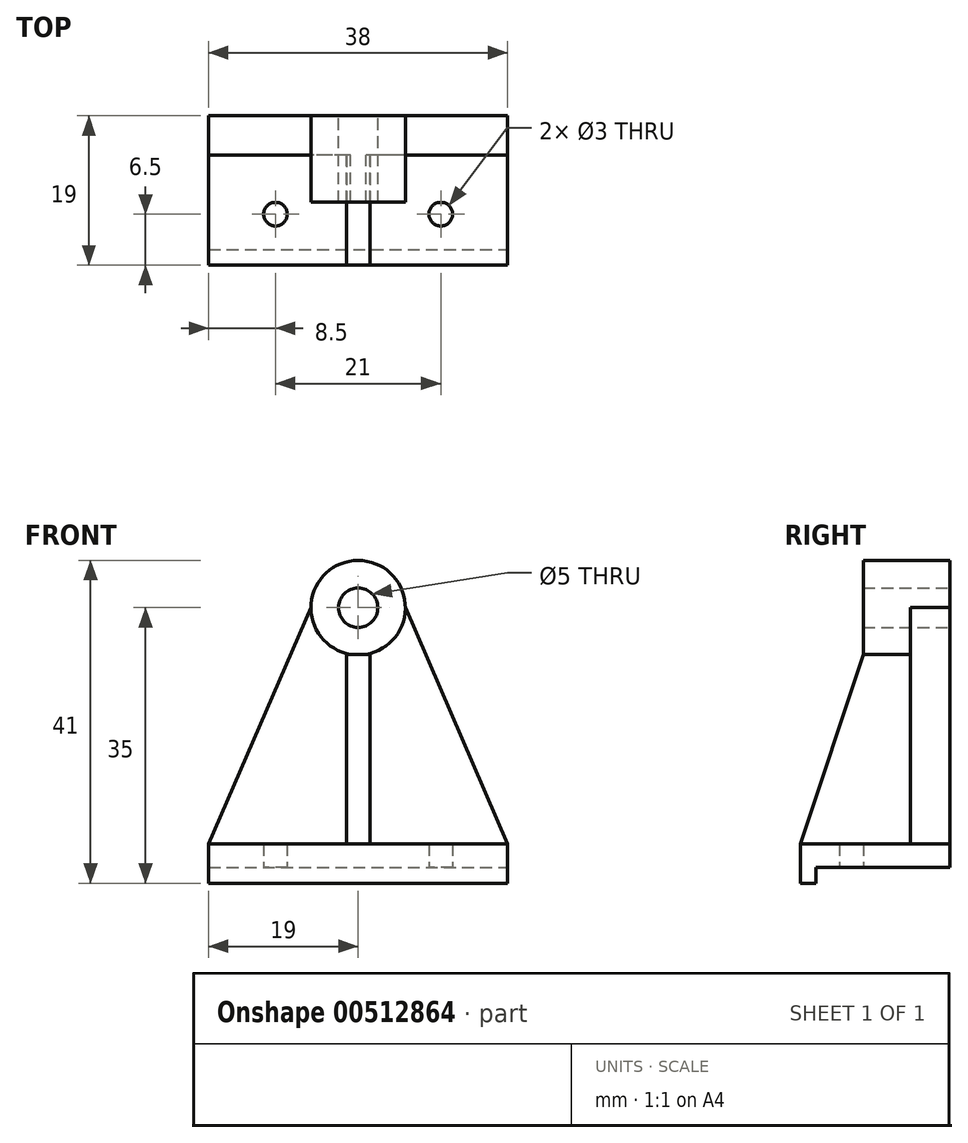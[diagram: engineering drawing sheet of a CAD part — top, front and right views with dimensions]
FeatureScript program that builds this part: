
annotation { "Feature Type Name" : "Feature", "Feature Type Description" : "" }
export const myFeature = defineFeature(function(context is Context, id is Id, definition is map)
    precondition{}
    {
        {
            var Q0;
            Q0=qCreatedBy(makeId("Top.planeOp"),FACE);
            var sketch = newSketch(context, id + "F0", { "sketchPlane" : qUnion([Q0])});
            skLineSegment(sketch, "E0.bottom", {"start": v(19, -9.5) * mm, "end": v(-19, -9.5) * mm});
            skLineSegment(sketch, "E0.top", {"start": v(19, 9.5) * mm, "end": v(-19, 9.5) * mm});
            skLineSegment(sketch, "E0.left", {"start": v(19, -9.5) * mm, "end": v(19, 9.5) * mm});
            skLineSegment(sketch, "E0.right", {"start": v(-19, -9.5) * mm, "end": v(-19, 9.5) * mm});
            skPoint(sketch, "E0.middle", {"position": v(0, 0) * mm});
            skCircle(sketch, "E1", {"center": v(10.5, -3) * mm, "radius": 1.5 * mm});
            skLineSegment(sketch, "E2", {"start": v(0, 0) * mm, "end": v(0, -4.4) * mm, "construction": true});
            skCircle(sketch, "E3.MirrorC", {"center": v(-10.5, -3) * mm, "radius": 1.5 * mm});
            skSolve(sketch);
        }
        {
            var Q0;
            Q0 = qSketchRegion(id + "F0", true);
            extrude(context, id + "F1", {"entities" : qUnion([Q0]), "depth" : 3 * mm});
        }
        {
            var Q0;
            Q0=makeQuery(id+"F1.opExtrude","SWEPT_FACE",FACE,{"disambiguationData":[OSD([sQuery(id+"F0.wireOp",EDGE,"E0.left")])]});
            var sketch = newSketch(context, id + "F2", { "sketchPlane" : qUnion([Q0])});
            skLineSegment(sketch, "E4.bottom", {"start": v(-9.5, 0) * mm, "end": v(-7.5, 0) * mm});
            skLineSegment(sketch, "E4.top", {"start": v(-9.5, -2) * mm, "end": v(-7.5, -2) * mm});
            skLineSegment(sketch, "E4.left", {"start": v(-9.5, 0) * mm, "end": v(-9.5, -2) * mm});
            skLineSegment(sketch, "E4.right", {"start": v(-7.5, 0) * mm, "end": v(-7.5, -2) * mm});
            skSolve(sketch);
        }
        {
            var Q0;
            Q0 = qSketchRegion(id + "F2", true);
            extrude(context, id + "F3", {"entities" : qUnion([Q0]), "operationType" : NewBodyOperationType.ADD, "oppositeDirection" : true, "depth" : 38 * mm});
        }
        {
            var Q0;
            Q0=makeQuery(id+"F1.opExtrude","SWEPT_FACE",FACE,{"disambiguationData":[OSD([sQuery(id+"F0.wireOp",EDGE,"E0.top")])]});
            var sketch = newSketch(context, id + "F4", { "sketchPlane" : qUnion([Q0])});
            skCircle(sketch, "E5", {"center": v(0, 33) * mm, "radius": 2.5 * mm});
            skCircle(sketch, "E6", {"center": v(0, 33) * mm, "radius": 6 * mm});
            skLineSegment(sketch, "E7", {"start": v(-19, 3) * mm, "end": v(-6, 33) * mm});
            skLineSegment(sketch, "E8", {"start": v(-6, 33) * mm, "end": v(6, 33) * mm});
            skLineSegment(sketch, "E9", {"start": v(6, 33) * mm, "end": v(19, 3) * mm});
            skSolve(sketch);
        }
        {
            var Q0;
            {var subQ1=sQuery(id+"F4.wireOp",EDGE,"E7");Q0=makeQuery(id+"F4.imprint","IMPRINT",FACE,{"disambiguationData":[TD([[makeQuery(id+"F4.imprint","IMPRINT",EDGE,{"derivedFrom":subQ1}),-1.0]])]});}
            extrude(context, id + "F5", {"entities" : qUnion([Q0]), "operationType" : NewBodyOperationType.ADD, "oppositeDirection" : true, "depth" : 5 * mm});
        }
        {
            var Q0;
            {var subQ0=sQuery(id+"F4.wireOp",EDGE,"E8");var subQ1=sQuery(id+"F4.wireOp",EDGE,"E5");var subQ2=makeQuery(id+"F4.imprint","INTERSECT",VERTEX,{"disambiguationData":[OD(0.0)],"derivedFrom":[subQ1,subQ0]});Q0=makeQuery(id+"F4.imprint","IMPRINT",FACE,{"disambiguationData":[TD([[makeQuery(id+"F4.imprint","IMPRINT",EDGE,{"disambiguationData":[TD([[subQ2,-1.0]])],"derivedFrom":subQ1}),-1.0]])]});}
            var Q1;
            {var subQ0=sQuery(id+"F4.wireOp",EDGE,"E8");var subQ1=sQuery(id+"F4.wireOp",EDGE,"E5");var subQ2=makeQuery(id+"F4.imprint","INTERSECT",VERTEX,{"disambiguationData":[OD(0.0)],"derivedFrom":[subQ1,subQ0]});Q1=makeQuery(id+"F4.imprint","IMPRINT",FACE,{"disambiguationData":[TD([[makeQuery(id+"F4.imprint","IMPRINT",EDGE,{"disambiguationData":[TD([[subQ2,1.0]])],"derivedFrom":subQ1}),-1.0]])]});}
            extrude(context, id + "F6", {"entities" : qUnion([Q0, Q1]), "operationType" : NewBodyOperationType.ADD, "oppositeDirection" : true, "depth" : 11 * mm});
        }
        {
            var Q0;
            Q0=qCreatedBy(makeId("Right.planeOp"),FACE);
            var sketch = newSketch(context, id + "F7", { "sketchPlane" : qUnion([Q0])});
            skLineSegment(sketch, "E10", {"start": v(-9.5, 3) * mm, "end": v(-1.5, 27.08) * mm});
            skLineSegment(sketch, "E11", {"start": v(-1.5, 27.08) * mm, "end": v(4.5, 27.08) * mm});
            skLineSegment(sketch, "E12", {"start": v(4.5, 27.08) * mm, "end": v(4.5, 3) * mm});
            skLineSegment(sketch, "E13", {"start": v(4.5, 3) * mm, "end": v(-9.5, 3) * mm});
            skSolve(sketch);
        }
        {
            var Q0;
            Q0 = qSketchRegion(id + "F7", true);
            extrude(context, id + "F8", {"entities" : qUnion([Q0]), "operationType" : NewBodyOperationType.ADD, "endBound" : BoundingType.SYMMETRIC, "depth" : 3 * mm});
        }
    });
